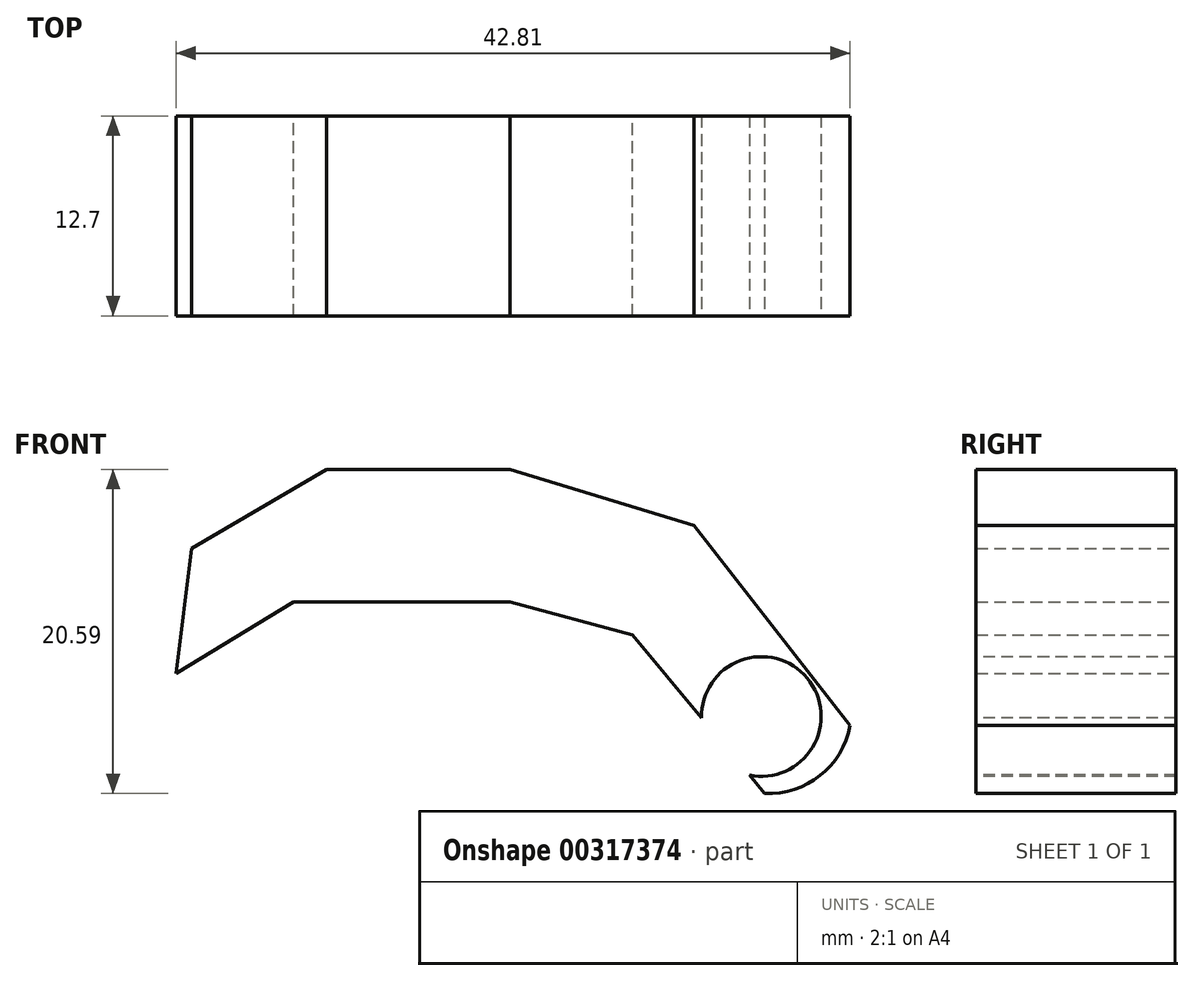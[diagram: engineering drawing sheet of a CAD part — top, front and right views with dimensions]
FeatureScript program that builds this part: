
annotation { "Feature Type Name" : "Feature", "Feature Type Description" : "" }
export const myFeature = defineFeature(function(context is Context, id is Id, definition is map)
    precondition{}
    {
        {
            var Q0;
            Q0=qCreatedBy(makeId("Front.planeOp"),FACE);
            var sketch = newSketch(context, id + "F0", { "sketchPlane" : qUnion([Q0])});
            skLineSegment(sketch, "E0", {"start": v(0, 0) * mm, "end": v(7.77, -2.1) * mm});
            skLineSegment(sketch, "E1", {"start": v(7.77, -2.1) * mm, "end": v(20.73, -17.65) * mm});
            skLineSegment(sketch, "E2", {"start": v(0, 0) * mm, "end": v(0, 8.42) * mm});
            skLineSegment(sketch, "E3", {"start": v(0, 8.42) * mm, "end": v(11.66, 4.86) * mm});
            skLineSegment(sketch, "E4", {"start": v(11.66, 4.86) * mm, "end": v(23.39, -10.16) * mm});
            skLineSegment(sketch, "E5", {"start": v(23.39, -10.16) * mm, "end": v(20.73, -17.65) * mm});
            skLineSegment(sketch, "E6", {"start": v(0, 0) * mm, "end": v(-13.77, 0) * mm});
            skLineSegment(sketch, "E7", {"start": v(-13.77, 0) * mm, "end": v(-21.22, -4.53) * mm});
            skLineSegment(sketch, "E8", {"start": v(0, 8.42) * mm, "end": v(-11.66, 8.42) * mm});
            skLineSegment(sketch, "E9", {"start": v(-11.66, 8.42) * mm, "end": v(-20.25, 3.4) * mm});
            skLineSegment(sketch, "E10", {"start": v(-21.22, -4.53) * mm, "end": v(-20.25, 3.4) * mm});
            skSolve(sketch);
        }
        {
            var Q0;
            Q0=makeQuery(id+"F0.imprint","IMPRINT",FACE,{"disambiguationData":[TD([[makeQuery(id+"F0.imprint","IMPRINT",EDGE,{"derivedFrom":sQuery(id+"F0.wireOp",EDGE,"E2")}),1.0]])]});
            var Q1;
            Q1=makeQuery(id+"F0.imprint","IMPRINT",FACE,{"disambiguationData":[TD([[makeQuery(id+"F0.imprint","IMPRINT",EDGE,{"derivedFrom":sQuery(id+"F0.wireOp",EDGE,"E0")}),1.0]])]});
            extrude(context, id + "F1", {"entities" : qUnion([Q0, Q1]), "depth" : 12.7 * mm});
        }
        {
            var Q0;
            Q0=makeQuery(id+"F1.opExtrude","CAP_FACE",FACE,{"disambiguationData":[OSD([sQuery(id+"F0.wireOp",EDGE,"E0"),sQuery(id+"F0.wireOp",EDGE,"E1"),sQuery(id+"F0.wireOp",EDGE,"E3"),sQuery(id+"F0.wireOp",EDGE,"E4"),sQuery(id+"F0.wireOp",EDGE,"E5"),sQuery(id+"F0.wireOp",EDGE,"E6"),sQuery(id+"F0.wireOp",EDGE,"E7"),sQuery(id+"F0.wireOp",EDGE,"E8"),sQuery(id+"F0.wireOp",EDGE,"E9"),sQuery(id+"F0.wireOp",EDGE,"E10")])],"isStart":false});
            var sketch = newSketch(context, id + "F2", { "sketchPlane" : qUnion([Q0])});
            skLineSegment(sketch, "E11", {"start": v(0, 0) * mm, "end": v(15.95, -7.27) * mm});
            skSolve(sketch);
        }
        {
            var Q0;
            Q0=sQuery(id+"F2.wireOp",VERTEX,"E11.end");
            var Q1;
            Q1=makeQuery(id+"F1.opExtrude","SWEPT_BODY",BODY,{"disambiguationData":[OSD([sQuery(id+"F0.wireOp",EDGE,"E0"),sQuery(id+"F0.wireOp",EDGE,"E1"),sQuery(id+"F0.wireOp",EDGE,"E3"),sQuery(id+"F0.wireOp",EDGE,"E4"),sQuery(id+"F0.wireOp",EDGE,"E5"),sQuery(id+"F0.wireOp",EDGE,"E6"),sQuery(id+"F0.wireOp",EDGE,"E7"),sQuery(id+"F0.wireOp",EDGE,"E8"),sQuery(id+"F0.wireOp",EDGE,"E9"),sQuery(id+"F0.wireOp",EDGE,"E10")])]});
            hole(context, id + "F3", {"style" : HoleStyle.SIMPLE, "endStyle" : HoleEndStyle.THROUGH, "holeDiameter" : 7.6 * mm, "tappedDepth" : 12.7 * mm, "tapClearance" : 3, "locations" : qUnion([Q0]), "scope" : qUnion([Q1])});
        }
        {
            var Q0;
            Q0=makeQuery(id+"F1.opExtrude","CAP_FACE",FACE,{"disambiguationData":[OSD([sQuery(id+"F0.wireOp",EDGE,"E0"),sQuery(id+"F0.wireOp",EDGE,"E1"),sQuery(id+"F0.wireOp",EDGE,"E3"),sQuery(id+"F0.wireOp",EDGE,"E4"),sQuery(id+"F0.wireOp",EDGE,"E5"),sQuery(id+"F0.wireOp",EDGE,"E6"),sQuery(id+"F0.wireOp",EDGE,"E7"),sQuery(id+"F0.wireOp",EDGE,"E8"),sQuery(id+"F0.wireOp",EDGE,"E9"),sQuery(id+"F0.wireOp",EDGE,"E10")])],"isStart":false});
            var sketch = newSketch(context, id + "F4", { "sketchPlane" : qUnion([Q0])});
            skArc(sketch, "E12", {"start": v(16.15, -12.16) * mm, "mid": v(19.68, -11.03) * mm, "end": v(21.59, -7.85) * mm});
            skSolve(sketch);
        }
        {
            var Q0;
            {var subQ0=sQuery(id+"F4.wireOp",EDGE,"E12");Q0=makeQuery(id+"F4.imprint","IMPRINT",FACE,{"disambiguationData":[TD([[makeQuery(id+"F4.imprint","IMPRINT",EDGE,{"derivedFrom":subQ0}),-1.0]])]});}
            extrude(context, id + "F5", {"entities" : qUnion([Q0]), "operationType" : NewBodyOperationType.REMOVE, "oppositeDirection" : true, "depth" : 25.4 * mm});
        }
    });
